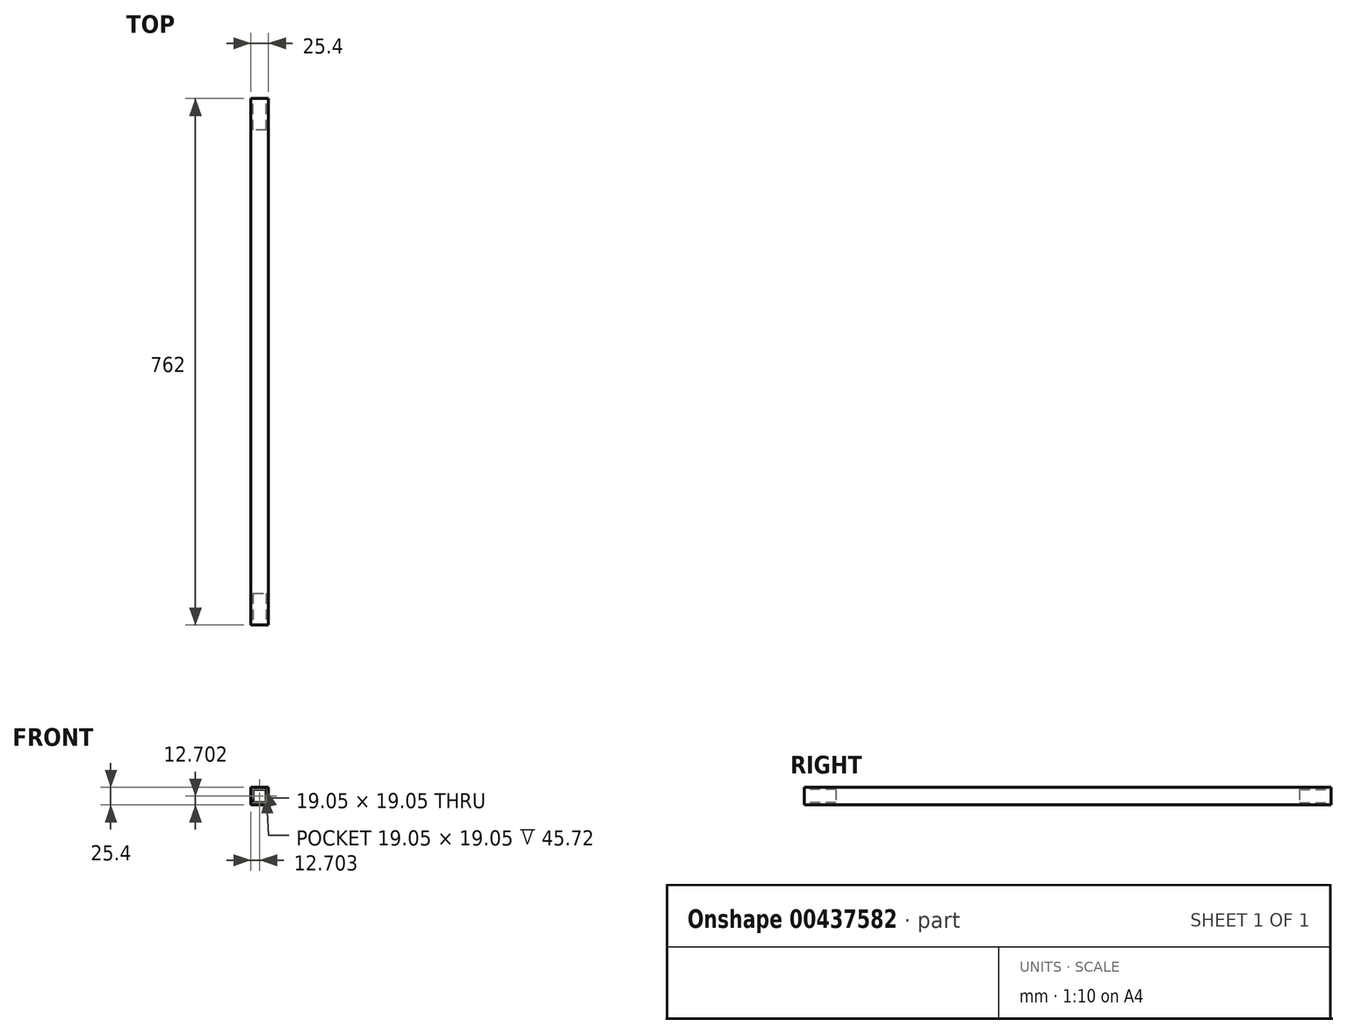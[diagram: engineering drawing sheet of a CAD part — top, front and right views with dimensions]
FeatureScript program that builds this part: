
annotation { "Feature Type Name" : "Feature", "Feature Type Description" : "" }
export const myFeature = defineFeature(function(context is Context, id is Id, definition is map)
    precondition{}
    {
        {
            var Q0;
            Q0=qCreatedBy(makeId("Front.planeOp"),FACE);
            var sketch = newSketch(context, id + "F0", { "sketchPlane" : qUnion([Q0])});
            skLineSegment(sketch, "E0.bottom", {"start": v(-13.18, 13) * mm, "end": v(12.22, 13) * mm});
            skLineSegment(sketch, "E0.top", {"start": v(-13.18, -12.4) * mm, "end": v(12.22, -12.4) * mm});
            skLineSegment(sketch, "E0.left", {"start": v(-13.18, 13) * mm, "end": v(-13.18, -12.4) * mm});
            skLineSegment(sketch, "E0.right", {"start": v(12.22, 13) * mm, "end": v(12.22, -12.4) * mm});
            skSolve(sketch);
        }
        {
            var Q0;
            Q0=makeQuery(id+"F0.imprint","IMPRINT",FACE,{"disambiguationData":[TD([[makeQuery(id+"F0.imprint","IMPRINT",EDGE,{"derivedFrom":sQuery(id+"F0.wireOp",EDGE,"E0.bottom")}),-1.0]])]});
            extrude(context, id + "F1", {"entities" : qUnion([Q0]), "depth" : 762 * mm});
        }
        {
            var Q0;
            Q0=makeQuery(id+"F1.opExtrude","CAP_FACE",FACE,{"disambiguationData":[OSD([sQuery(id+"F0.wireOp",EDGE,"E0.bottom"),sQuery(id+"F0.wireOp",EDGE,"E0.top"),sQuery(id+"F0.wireOp",EDGE,"E0.left"),sQuery(id+"F0.wireOp",EDGE,"E0.right")])],"isStart":false});
            var sketch = newSketch(context, id + "F2", { "sketchPlane" : qUnion([Q0])});
            skLineSegment(sketch, "E1.bottom", {"start": v(-10, 9.83) * mm, "end": v(9.05, 9.83) * mm});
            skLineSegment(sketch, "E1.top", {"start": v(-10, -9.22) * mm, "end": v(9.05, -9.22) * mm});
            skLineSegment(sketch, "E1.left", {"start": v(-10, 9.83) * mm, "end": v(-10, -9.22) * mm});
            skLineSegment(sketch, "E1.right", {"start": v(9.05, 9.83) * mm, "end": v(9.05, -9.22) * mm});
            skSolve(sketch);
        }
        {
            var Q0;
            Q0 = qSketchRegion(id + "F2", true);
            extrude(context, id + "F3", {"entities" : qUnion([Q0]), "operationType" : NewBodyOperationType.REMOVE, "oppositeDirection" : true, "depth" : 45.72 * mm});
        }
        {
            var Q0;
            Q0=makeQuery(id+"F1.opExtrude","CAP_FACE",FACE,{"disambiguationData":[OSD([sQuery(id+"F0.wireOp",EDGE,"E0.bottom"),sQuery(id+"F0.wireOp",EDGE,"E0.top"),sQuery(id+"F0.wireOp",EDGE,"E0.left"),sQuery(id+"F0.wireOp",EDGE,"E0.right")])],"isStart":true});
            var sketch = newSketch(context, id + "F4", { "sketchPlane" : qUnion([Q0])});
            skLineSegment(sketch, "E2.bottom", {"start": v(-9.05, 9.83) * mm, "end": v(10, 9.83) * mm});
            skLineSegment(sketch, "E2.top", {"start": v(-9.05, -9.22) * mm, "end": v(10, -9.22) * mm});
            skLineSegment(sketch, "E2.left", {"start": v(-9.05, 9.83) * mm, "end": v(-9.05, -9.22) * mm});
            skLineSegment(sketch, "E2.right", {"start": v(10, 9.83) * mm, "end": v(10, -9.22) * mm});
            skSolve(sketch);
        }
        {
            var Q0;
            Q0=makeQuery(id+"F4.imprint","IMPRINT",FACE,{"disambiguationData":[TD([[makeQuery(id+"F4.imprint","IMPRINT",EDGE,{"derivedFrom":sQuery(id+"F4.wireOp",EDGE,"E2.bottom")}),-1.0]])]});
            extrude(context, id + "F5", {"entities" : qUnion([Q0]), "operationType" : NewBodyOperationType.REMOVE, "oppositeDirection" : true, "depth" : 45.72 * mm});
        }
    });
